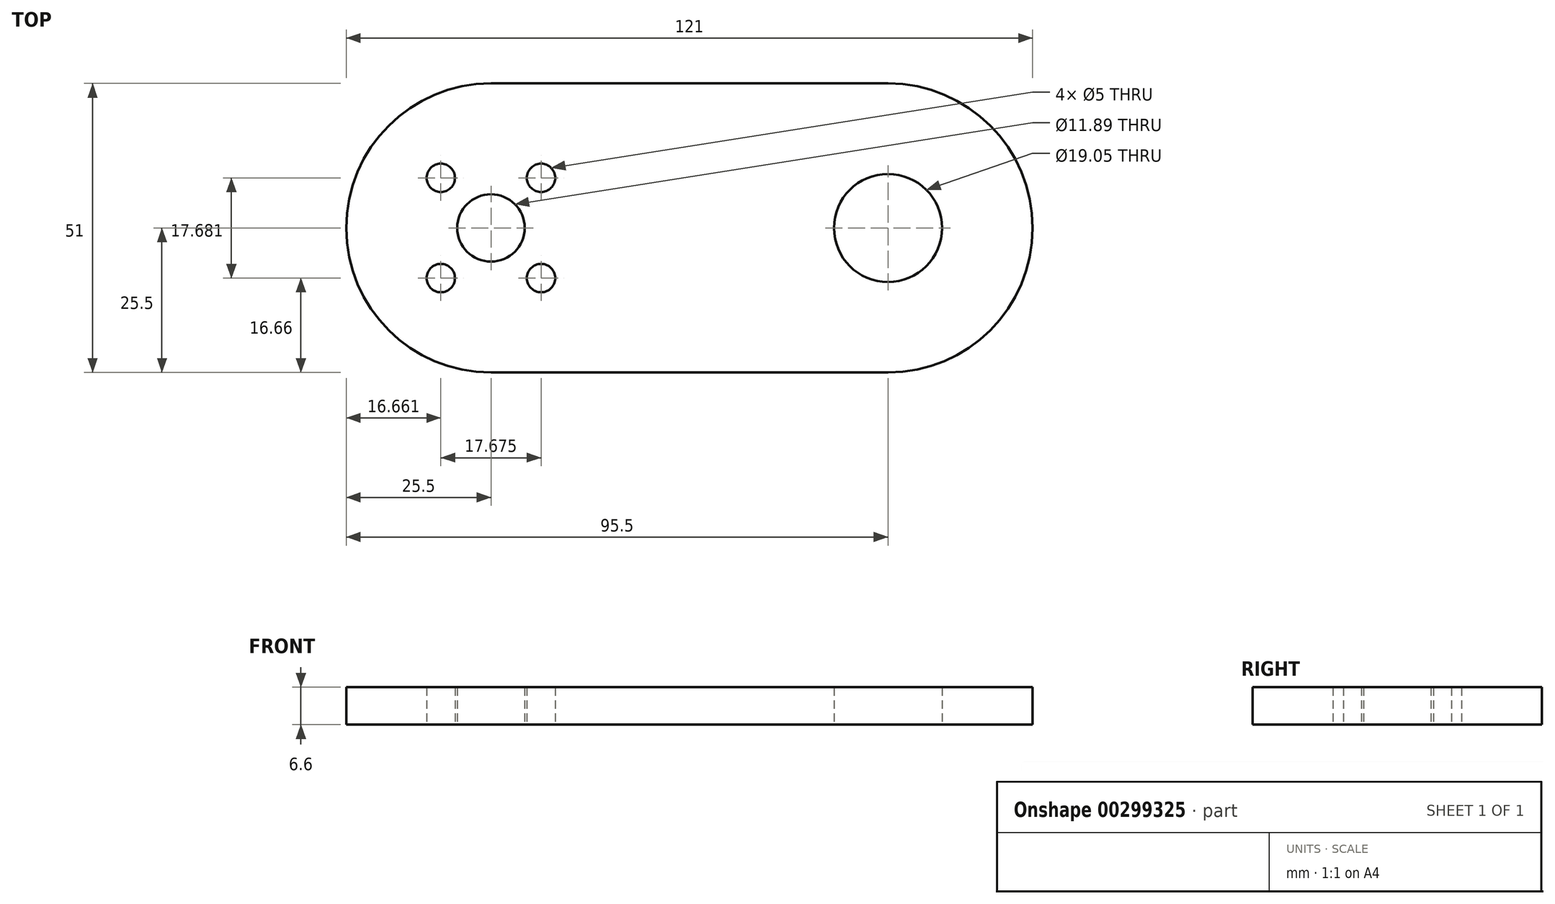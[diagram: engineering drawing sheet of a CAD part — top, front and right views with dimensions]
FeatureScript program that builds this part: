
annotation { "Feature Type Name" : "Feature", "Feature Type Description" : "" }
export const myFeature = defineFeature(function(context is Context, id is Id, definition is map)
    precondition{}
    {
        {
            var Q0;
            Q0=qCreatedBy(makeId("Top.planeOp"),FACE);
            var sketch = newSketch(context, id + "F0", { "sketchPlane" : qUnion([Q0])});
            skLineSegment(sketch, "E0.bottom", {"start": v(35, 25.5) * mm, "end": v(-35, 25.5) * mm});
            skLineSegment(sketch, "E0.top", {"start": v(35, -25.5) * mm, "end": v(-35, -25.5) * mm});
            skLineSegment(sketch, "E0.left", {"start": v(35, 25.5) * mm, "end": v(35, -25.5) * mm});
            skLineSegment(sketch, "E0.right", {"start": v(-35, 25.5) * mm, "end": v(-35, -25.5) * mm});
            skPoint(sketch, "E0.middle", {"position": v(0, 0) * mm});
            skArc(sketch, "E1", {"start": v(-35, 25.5) * mm, "mid": v(-60.5, 0) * mm, "end": v(-35, -25.5) * mm});
            skArc(sketch, "E2", {"start": v(35, -25.5) * mm, "mid": v(60.5, 0) * mm, "end": v(35, 25.5) * mm});
            skCircle(sketch, "E3", {"center": v(35, 0) * mm, "radius": 9.53 * mm});
            skCircle(sketch, "E4", {"center": v(-35, 0) * mm, "radius": 5943.6 * mm});
            skLineSegment(sketch, "E5", {"start": v(-35, 0) * mm, "end": v(-43.84, 8.84) * mm});
            skCircle(sketch, "E6", {"center": v(-43.84, 8.84) * mm, "radius": 2.5 * mm});
            skLineSegment(sketch, "E7", {"start": v(-43.84, 8.84) * mm, "end": v(-43.84, -8.84) * mm});
            skCircle(sketch, "E8", {"center": v(-43.84, -8.84) * mm, "radius": 2.5 * mm});
            skLineSegment(sketch, "E9", {"start": v(-35, 0) * mm, "end": v(-26.16, -8.84) * mm});
            skCircle(sketch, "E10", {"center": v(-26.16, -8.84) * mm, "radius": 2.5 * mm});
            skLineSegment(sketch, "E11", {"start": v(-26.16, -8.84) * mm, "end": v(-26.16, 8.84) * mm});
            skCircle(sketch, "E12", {"center": v(-26.16, 8.84) * mm, "radius": 2.5 * mm});
            skCircle(sketch, "E13", {"center": v(-35, 0) * mm, "radius": 5.94 * mm});
            skSolve(sketch);
        }
        {
            var Q0;
            {var subQ0=sQuery(id+"F0.wireOp",EDGE,"E1");Q0=makeQuery(id+"F0.imprint","IMPRINT",FACE,{"disambiguationData":[TD([[makeQuery(id+"F0.imprint","IMPRINT",EDGE,{"derivedFrom":subQ0}),1.0]])]});}
            var Q1;
            {var subQ6=sQuery(id+"F0.wireOp",EDGE,"E0.bottom");Q1=makeQuery(id+"F0.imprint","IMPRINT",FACE,{"disambiguationData":[TD([[makeQuery(id+"F0.imprint","IMPRINT",EDGE,{"derivedFrom":subQ6}),1.0]])]});}
            var Q2;
            {var subQ0=sQuery(id+"F0.wireOp",EDGE,"E2");Q2=makeQuery(id+"F0.imprint","IMPRINT",FACE,{"disambiguationData":[TD([[makeQuery(id+"F0.imprint","IMPRINT",EDGE,{"derivedFrom":subQ0}),1.0]])]});}
            extrude(context, id + "F1", {"entities" : qUnion([Q0, Q1, Q2]), "depth" : 6.6 * mm});
        }
    });
